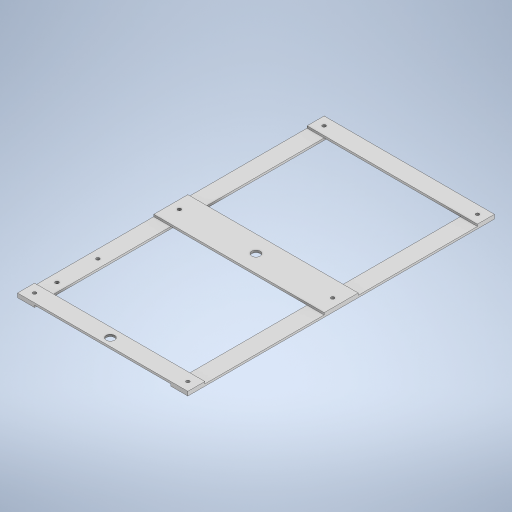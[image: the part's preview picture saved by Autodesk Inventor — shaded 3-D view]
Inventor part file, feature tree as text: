
AUTODESK INVENTOR PART (.ipt)
format: ipt  version: 2024 (Build 280153000, 153)  size: 386,560 bytes
history: native  units: mm
features: extrude x10, sketch x10, thread x9
ambient origin geometry x8: Origin, YZ Plane, XZ Plane, XY Plane, X Axis, Y Axis, Z Axis, Center Point
bodies: Solid1 (feature_tree)
feature tree (29):
  extrude  "Extrusion1"  Depth=3.0mm
  extrude  "Extrusion2"  Depth=250.0mm
  extrude  "Extrusion3"  Depth=3.0mm TaperAngle=0.0deg
  extrude  "Extrusion4"  Depth=25.0mm
  extrude  "Extrusion5"  Depth=25.0mm
  extrude  "Extrusion6"  Depth=3.0mm TaperAngle=0.0deg
  extrude  "Extrusion7"  Depth=250.0mm
  thread  "Thread1"  [1 undecoded]
  thread  "Thread2"  [1 undecoded]
  thread  "Thread3"  [1 undecoded]
  thread  "Thread4"  [1 undecoded]
  thread  "Thread5"  [1 undecoded]
  thread  "Thread6"  [1 undecoded]
  extrude  "Extrusion8"  Depth=5.0mm
  extrude  "Extrusion9"  Depth=25.0mm
  thread  "Thread7"  [1 undecoded]
  extrude  "Extrusion10"  Depth=25.0mm
  thread  "Thread8"  [1 undecoded]
  thread  "Thread9"  [1 undecoded]
  sketch  "Sketch1"  dims[d0=25.0mm d1=3.0mm]
  sketch  "Sketch2"  dims[d2=450.0mm d3=0.0mm d4=250.0mm]
  sketch  "Sketch3"  dims[d5=25.0mm d6=3.0mm d7=0.0mm]
  sketch  "Sketch4"  dims[d8=250.0mm d9=25.0mm]
  sketch  "Sketch5"  dims[d10=3.0mm d11=0.0mm d12=25.0mm]
  sketch  "Sketch6"  dims[d13=450.0mm d14=3.0mm d15=0.0mm]
  sketch  "Sketch7"  dims[d16=200.0mm d17=250.0mm d18=50.0mm d19=3.0mm d20=0.0mm d21=5.0mm d22=5.0mm d23=5.0mm d24=5.0mm]
  sketch  "Sketch8"  dims[d25=100.0mm d26=0.0mm d27=5.0mm]
  sketch  "Sketch9"  dims[d28=12.5mm d29=25.0mm d30=5.0mm]
  sketch  "Sketch10"  dims[d31=12.5mm d32=25.0mm d33=100.0mm d34=0.0mm d35=6.0mm d36=0.0mm d37=6.0mm d38=0.0mm d39=6.0mm d40=0.0mm d41=6.0mm d42=0.0mm d43=6.0mm d44=0.0mm d45=6.0mm d46=0.0mm d47=12.7mm d48=125.0mm d49=10.0mm d50=0.0mm d51=12.7mm d52=125.0mm d53=0.0mm d54=0.0mm d55=3.0mm d56=0.0mm d57=100.0mm d58=5.0mm d59=5.0mm d60=20.0mm d61=20.0mm d62=12.5mm d63=12.5mm d64=10.0mm d65=0.0mm d66=3.0mm d67=0.0mm d68=3.0mm d69=0.0mm]
note: 9 required parameter values undecoded (feature->parameter linkage not recoverable at this tier; creation-order binding heuristic only, values carry confidence <= 0.55)
